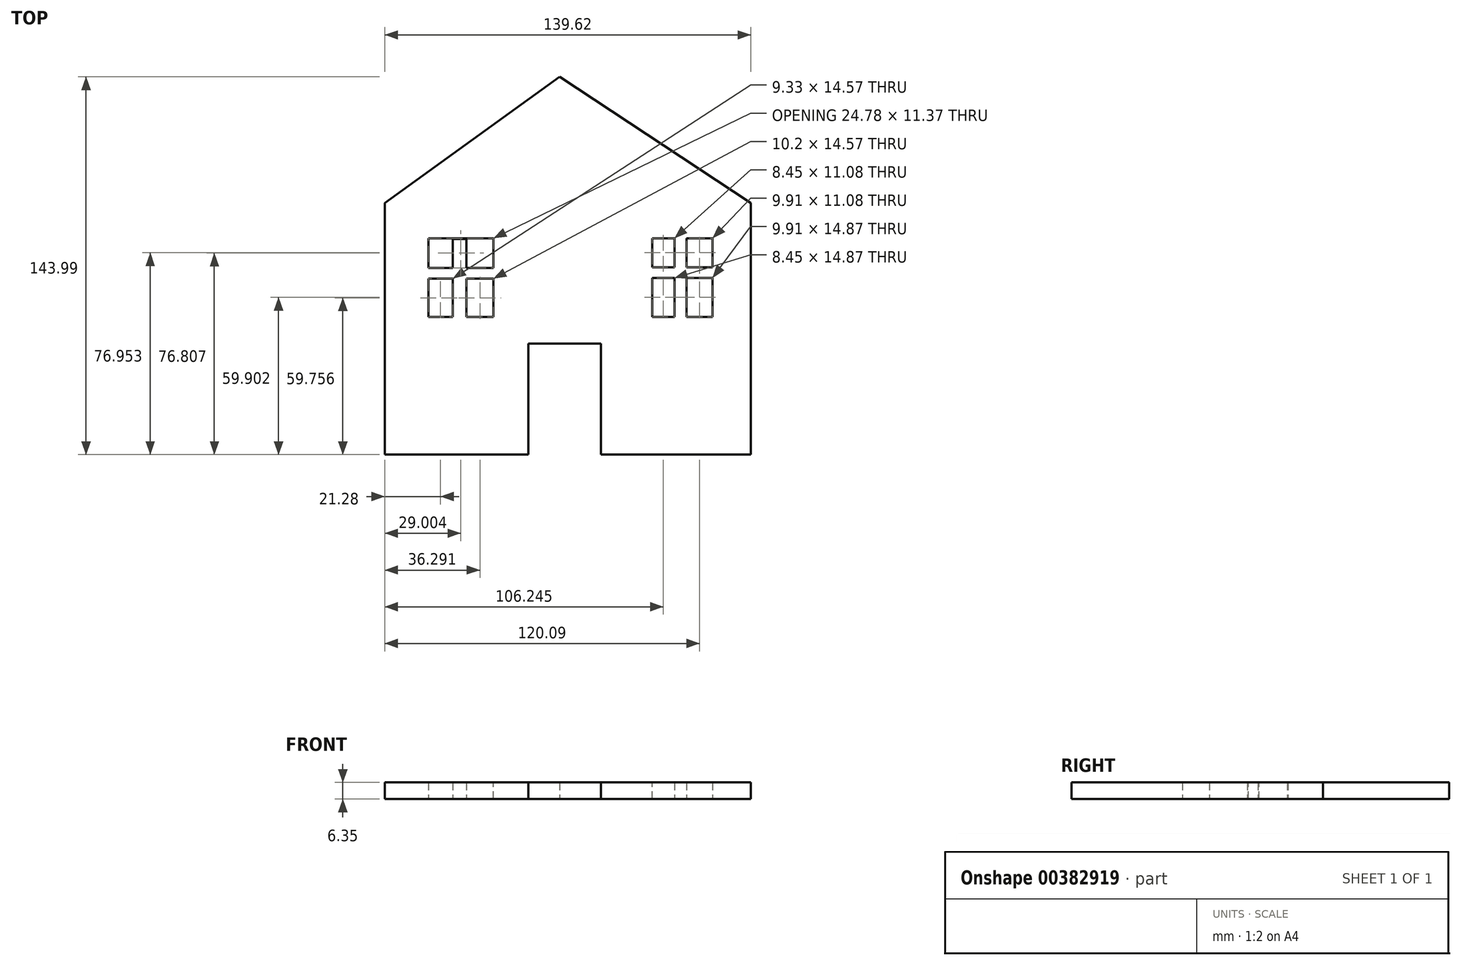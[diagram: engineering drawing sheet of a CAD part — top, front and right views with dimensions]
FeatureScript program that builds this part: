
annotation { "Feature Type Name" : "Feature", "Feature Type Description" : "" }
export const myFeature = defineFeature(function(context is Context, id is Id, definition is map)
    precondition{}
    {
        {
            var Q0;
            Q0=qCreatedBy(makeId("Top.planeOp"),FACE);
            var sketch = newSketch(context, id + "F0", { "sketchPlane" : qUnion([Q0])});
            skLineSegment(sketch, "E0.bottom", {"start": v(-66.75, 28.42) * mm, "end": v(72.87, 28.42) * mm});
            skLineSegment(sketch, "E0.top", {"start": v(-66.75, -67.48) * mm, "end": v(72.87, -67.48) * mm});
            skLineSegment(sketch, "E0.left", {"start": v(-66.75, 28.42) * mm, "end": v(-66.75, -67.48) * mm});
            skLineSegment(sketch, "E0.right", {"start": v(72.87, 28.42) * mm, "end": v(72.87, -67.48) * mm});
            skLineSegment(sketch, "E1", {"start": v(-66.75, 28.42) * mm, "end": v(0, 76.51) * mm});
            skLineSegment(sketch, "E2", {"start": v(0, 76.51) * mm, "end": v(72.87, 28.42) * mm});
            skLineSegment(sketch, "E3", {"start": v(-50.13, 15.01) * mm, "end": v(-50.13, -15.01) * mm});
            skLineSegment(sketch, "E4", {"start": v(-50.13, -15.01) * mm, "end": v(-25.36, -15.01) * mm});
            skLineSegment(sketch, "E5", {"start": v(-25.36, -15.01) * mm, "end": v(-25.36, 15.01) * mm});
            skLineSegment(sketch, "E6", {"start": v(-25.36, 15.01) * mm, "end": v(-50.13, 15.01) * mm});
            skLineSegment(sketch, "E7", {"start": v(-37.75, 15.01) * mm, "end": v(-37.75, -15.01) * mm});
            skLineSegment(sketch, "E8", {"start": v(-50.13, 0) * mm, "end": v(-37.75, 0) * mm});
            skLineSegment(sketch, "E9", {"start": v(-37.75, 0) * mm, "end": v(-25.36, 0) * mm});
            skLineSegment(sketch, "E10", {"start": v(35.27, 15.01) * mm, "end": v(58.3, 15.01) * mm});
            skLineSegment(sketch, "E11", {"start": v(58.3, 15.01) * mm, "end": v(58.3, -15.01) * mm});
            skLineSegment(sketch, "E12", {"start": v(58.3, -15.01) * mm, "end": v(35.27, -15.01) * mm});
            skLineSegment(sketch, "E13", {"start": v(35.27, -15.01) * mm, "end": v(35.27, 15.01) * mm});
            skLineSegment(sketch, "E14", {"start": v(46.78, 15.01) * mm, "end": v(46.78, -15.01) * mm});
            skLineSegment(sketch, "E15", {"start": v(35.27, 0) * mm, "end": v(46.78, 0) * mm});
            skLineSegment(sketch, "E16", {"start": v(58.3, 0) * mm, "end": v(46.78, 0) * mm});
            skLineSegment(sketch, "E17.bottom", {"start": v(-11.95, -25.21) * mm, "end": v(15.74, -25.21) * mm});
            skLineSegment(sketch, "E17.top", {"start": v(-11.95, -67.48) * mm, "end": v(15.74, -67.48) * mm});
            skLineSegment(sketch, "E17.left", {"start": v(-11.95, -25.21) * mm, "end": v(-11.95, -67.48) * mm});
            skLineSegment(sketch, "E17.right", {"start": v(15.74, -25.21) * mm, "end": v(15.74, -67.48) * mm});
            skCircle(sketch, "E18", {"center": v(9.62, -47.66) * mm, "radius": 2.1 * mm});
            skSolve(sketch);
        }
        {
            var Q0;
            Q0=makeQuery(id+"F0.imprint","IMPRINT",FACE,{"disambiguationData":[TD([[makeQuery(id+"F0.imprint","IMPRINT",EDGE,{"derivedFrom":sQuery(id+"F0.wireOp",EDGE,"E0.bottom")}),-1.0]])]});
            var Q1;
            Q1=makeQuery(id+"F0.imprint","IMPRINT",FACE,{"disambiguationData":[TD([[makeQuery(id+"F0.imprint","IMPRINT",EDGE,{"derivedFrom":sQuery(id+"F0.wireOp",EDGE,"E0.bottom")}),1.0]])]});
            extrude(context, id + "F1", {"entities" : qUnion([Q0, Q1]), "depth" : 6.35 * mm});
        }
        {
            var Q0;
            Q0=qCreatedBy(makeId("Top.planeOp"),FACE);
            var sketch = newSketch(context, id + "F2", { "sketchPlane" : qUnion([Q0])});
            skLineSegment(sketch, "E19.bottom", {"start": v(43.72, 15.6) * mm, "end": v(48.38, 15.6) * mm});
            skLineSegment(sketch, "E19.top", {"start": v(43.72, -15.89) * mm, "end": v(48.38, -15.89) * mm});
            skLineSegment(sketch, "E19.left", {"start": v(43.72, 15.6) * mm, "end": v(43.72, -15.89) * mm});
            skLineSegment(sketch, "E19.right", {"start": v(48.38, 15.6) * mm, "end": v(48.38, -15.89) * mm});
            skPoint(sketch, "E20.oppositeSnap0", {"position": v(43.72, -0.15) * mm});
            skLineSegment(sketch, "E20.bottom", {"start": v(59.17, 3.93) * mm, "end": v(33.52, 3.93) * mm});
            skLineSegment(sketch, "E20.top", {"start": v(59.17, -0.15) * mm, "end": v(33.52, -0.15) * mm});
            skLineSegment(sketch, "E20.left", {"start": v(59.17, 3.93) * mm, "end": v(59.17, -0.15) * mm});
            skLineSegment(sketch, "E20.right", {"start": v(33.52, 3.93) * mm, "end": v(33.52, -0.15) * mm});
            skSolve(sketch);
        }
        {
            var Q0;
            Q0 = qSketchRegion(id + "F2", true);
            extrude(context, id + "F3", {"entities" : qUnion([Q0]), "operationType" : NewBodyOperationType.ADD, "depth" : 6.35 * mm});
        }
        {
            var Q0;
            Q0=qCreatedBy(makeId("Top.planeOp"),FACE);
            var sketch = newSketch(context, id + "F4", { "sketchPlane" : qUnion([Q0])});
            skLineSegment(sketch, "E21.bottom", {"start": v(-40.8, 14.72) * mm, "end": v(-35.56, 14.72) * mm});
            skLineSegment(sketch, "E21.top", {"start": v(-40.8, -15.6) * mm, "end": v(-35.56, -15.6) * mm});
            skLineSegment(sketch, "E21.left", {"start": v(-40.8, 14.72) * mm, "end": v(-40.8, -15.6) * mm});
            skLineSegment(sketch, "E21.right", {"start": v(-35.56, 14.72) * mm, "end": v(-35.56, -15.6) * mm});
            skPoint(sketch, "E22.oppositeSnap0", {"position": v(-40.8, -0.44) * mm});
            skLineSegment(sketch, "E22.bottom", {"start": v(-25.07, 3.64) * mm, "end": v(-51.88, 3.64) * mm});
            skLineSegment(sketch, "E22.top", {"start": v(-25.07, -0.44) * mm, "end": v(-51.88, -0.44) * mm});
            skLineSegment(sketch, "E22.left", {"start": v(-25.07, 3.64) * mm, "end": v(-25.07, -0.44) * mm});
            skLineSegment(sketch, "E22.right", {"start": v(-51.88, 3.64) * mm, "end": v(-51.88, -0.44) * mm});
            skSolve(sketch);
        }
        {
            var Q0;
            Q0 = qSketchRegion(id + "F4", true);
            extrude(context, id + "F5", {"entities" : qUnion([Q0]), "operationType" : NewBodyOperationType.ADD, "depth" : 6.35 * mm});
        }
    });
